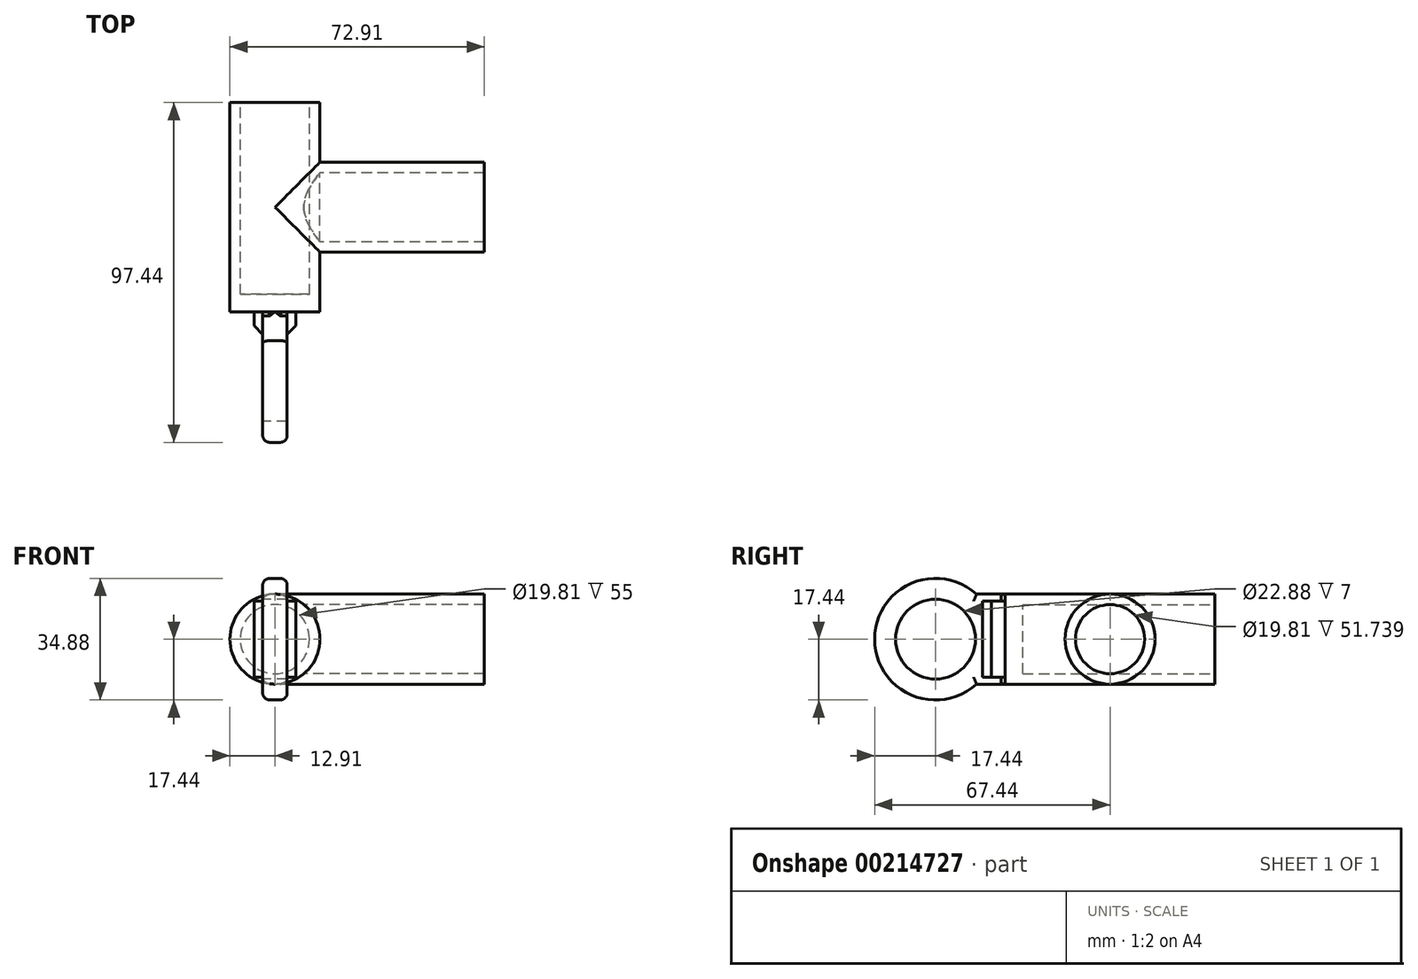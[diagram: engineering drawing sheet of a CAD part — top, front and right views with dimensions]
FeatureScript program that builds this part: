
annotation { "Feature Type Name" : "Feature", "Feature Type Description" : "" }
export const myFeature = defineFeature(function(context is Context, id is Id, definition is map)
    precondition{}
    {
        {
            assignVariable(context, id + "F0", {"name" : "ZZW", "anyValue" : 7});
        }
        {
            var Q0;
            Q0=qCreatedBy(makeId("Front.planeOp"),FACE);
            var sketch = newSketch(context, id + "F1", { "sketchPlane" : qUnion([Q0])});
            skCircle(sketch, "E0", {"center": v(0, 0) * mm, "radius": 9.9 * mm});
            skCircle(sketch, "E1", {"center": v(0, 0) * mm, "radius": 12.9 * mm});
            skSolve(sketch);
        }
        {
            var Q0;
            Q0=qSketchRegion(id+"F1",true);
            extrude(context, id + "F2", {"entities" : qUnion([Q0]), "depth" : 55 * mm});
        }
        {
            var Q0;
            Q0=makeQuery(id+"F2.opExtrude","CAP_FACE",FACE,{"disambiguationData":[OSD([sQuery(id+"F1.wireOp",EDGE,"E0"),sQuery(id+"F1.wireOp",EDGE,"E1")])],"isStart":false});
            var sketch = newSketch(context, id + "F3", { "sketchPlane" : qUnion([Q0])});
            skCircle(sketch, "E2", {"center": v(0, 0) * mm, "radius": 12.9 * mm});
            skSolve(sketch);
        }
        {
            var Q0;
            Q0=qSketchRegion(id+"F3",true);
            extrude(context, id + "F4", {"entities" : qUnion([Q0]), "operationType" : NewBodyOperationType.ADD, "depth" : 5 * mm});
        }
        {
            var Q0;
            Q0=qCreatedBy(makeId("Right.planeOp"),FACE);
            var sketch = newSketch(context, id + "F5", { "sketchPlane" : qUnion([Q0])});
            skLineSegment(sketch, "E3", {"start": v(0, 0) * mm, "end": v(0, -12.9) * mm, "construction": true});
            skLineSegment(sketch, "E4", {"start": v(0, -12.9) * mm, "end": v(-60, -12.9) * mm, "construction": true});
            skLineSegment(sketch, "E5", {"start": v(-60, 0) * mm, "end": v(-60, 12.9) * mm, "construction": true});
            skLineSegment(sketch, "E6", {"start": v(-60, -12.9) * mm, "end": v(-80, -12.9) * mm});
            skLineSegment(sketch, "E7", {"start": v(-80, -12.9) * mm, "end": v(-80, 12.9) * mm});
            skLineSegment(sketch, "E8", {"start": v(-80, 12.9) * mm, "end": v(-60, 12.9) * mm});
            skLineSegment(sketch, "E9", {"start": v(-60, -12.9) * mm, "end": v(-60, 12.9) * mm});
            skCircle(sketch, "E10", {"center": v(-80, 0) * mm, "radius": 11.44 * mm});
            skCircle(sketch, "E11", {"center": v(-80, 0) * mm, "radius": 17.44 * mm});
            skSolve(sketch);
        }
        {
            var Q0;
            {var subQ1=sQuery(id+"F5.wireOp",EDGE,"E7");var subQ5=sQuery(id+"F5.wireOp",EDGE,"E6");var subQ6=makeQuery(id+"F5.imprint","INTERSECT",VERTEX,{"derivedFrom":[subQ5,subQ1]});Q0=makeQuery(id+"F5.imprint","IMPRINT",FACE,{"disambiguationData":[TD([[makeQuery(id+"F5.imprint","IMPRINT",EDGE,{"disambiguationData":[TD([[subQ6,1.0]])],"derivedFrom":subQ5}),1.0]])]});}
            var Q1;
            {var subQ0=sQuery(id+"F5.wireOp",EDGE,"E9");Q1=makeQuery(id+"F5.imprint","IMPRINT",FACE,{"disambiguationData":[TD([[makeQuery(id+"F5.imprint","IMPRINT",EDGE,{"derivedFrom":subQ0}),1.0]])]});}
            var Q2;
            {var subQ1=sQuery(id+"F5.wireOp",EDGE,"E7");var subQ5=sQuery(id+"F5.wireOp",EDGE,"E6");var subQ6=makeQuery(id+"F5.imprint","INTERSECT",VERTEX,{"derivedFrom":[subQ5,subQ1]});Q2=makeQuery(id+"F5.imprint","IMPRINT",FACE,{"disambiguationData":[TD([[makeQuery(id+"F5.imprint","IMPRINT",EDGE,{"disambiguationData":[TD([[subQ6,1.0]])],"derivedFrom":subQ5}),-1.0]])]});}
            extrude(context, id + "F6", {"entities" : qUnion([Q0, Q1, Q2]), "operationType" : NewBodyOperationType.ADD, "depth" : (getVariable(context, 'ZZW') / 2) * mm, "hasSecondDirection" : true, "secondDirectionOppositeDirection" : true, "secondDirectionDepth" : (getVariable(context, 'ZZW') / 2) * mm});
        }
        {
            var Q0;
            {var subQ0=sQuery(id+"F5.wireOp",EDGE,"E9");var subQ1=sQuery(id+"F5.wireOp",EDGE,"E6");Q0=makeQuery(id+"F6.boolean.opBoolean","SPLIT",EDGE,{"disambiguationData":[TD([makeQuery(id+"F6.opExtrude","CAP_FACE",FACE,{"disambiguationData":[OSD([subQ1,sQuery(id+"F5.wireOp",EDGE,"E8"),subQ0,sQuery(id+"F5.wireOp",EDGE,"E10"),sQuery(id+"F5.wireOp",EDGE,"E11")])],"isStart":true})])],"derivedFrom":makeQuery(id+"F6.opExtrude","SWEPT_EDGE",EDGE,{"disambiguationData":[OSD([subQ1,subQ0])]})});}
            var Q1;
            {var subQ0=sQuery(id+"F5.wireOp",EDGE,"E6");var subQ1=sQuery(id+"F5.wireOp",EDGE,"E9");Q1=makeQuery(id+"F6.boolean.opBoolean","SPLIT",EDGE,{"disambiguationData":[TD([makeQuery(id+"F6.opExtrude","CAP_FACE",FACE,{"disambiguationData":[OSD([subQ0,sQuery(id+"F5.wireOp",EDGE,"E8"),subQ1,sQuery(id+"F5.wireOp",EDGE,"E10"),sQuery(id+"F5.wireOp",EDGE,"E11")])],"isStart":false})])],"derivedFrom":makeQuery(id+"F6.opExtrude","SWEPT_EDGE",EDGE,{"disambiguationData":[OSD([subQ0,subQ1])]})});}
            fillet(context, id + "F7", {"entities" : qUnion([Q0, Q1]), "radius" : 5 * mm, "tangentPropagation" : true, "allowEdgeOverflow" : false});
        }
        {
            var Q0;
            {var subQ0=sQuery(id+"F5.wireOp",EDGE,"E9");var subQ1=sQuery(id+"F5.wireOp",EDGE,"E8");Q0=makeQuery(id+"F6.boolean.opBoolean","SPLIT",EDGE,{"disambiguationData":[TD([makeQuery(id+"F6.opExtrude","CAP_FACE",FACE,{"disambiguationData":[OSD([sQuery(id+"F5.wireOp",EDGE,"E6"),subQ1,subQ0,sQuery(id+"F5.wireOp",EDGE,"E10"),sQuery(id+"F5.wireOp",EDGE,"E11")])],"isStart":true})])],"derivedFrom":makeQuery(id+"F6.opExtrude","SWEPT_EDGE",EDGE,{"disambiguationData":[OSD([subQ1,subQ0])]})});}
            var Q1;
            {var subQ0=sQuery(id+"F5.wireOp",EDGE,"E9");var subQ1=sQuery(id+"F5.wireOp",EDGE,"E8");Q1=makeQuery(id+"F6.boolean.opBoolean","SPLIT",EDGE,{"disambiguationData":[TD([makeQuery(id+"F6.opExtrude","CAP_FACE",FACE,{"disambiguationData":[OSD([sQuery(id+"F5.wireOp",EDGE,"E6"),subQ1,subQ0,sQuery(id+"F5.wireOp",EDGE,"E10"),sQuery(id+"F5.wireOp",EDGE,"E11")])],"isStart":false})])],"derivedFrom":makeQuery(id+"F6.opExtrude","SWEPT_EDGE",EDGE,{"disambiguationData":[OSD([subQ1,subQ0])]})});}
            fillet(context, id + "F8", {"entities" : qUnion([Q0, Q1]), "radius" : 5 * mm, "tangentPropagation" : true, "allowEdgeOverflow" : false});
        }
        {
            var Q0;
            Q0=makeQuery(id+"F6.opExtrude","CAP_EDGE",EDGE,{"disambiguationData":[OSD([sQuery(id+"F5.wireOp",EDGE,"E11")])],"isStart":true});
            fillet(context, id + "F9", {"entities" : qUnion([Q0]), "radius" : 2 * mm, "tangentPropagation" : true, "allowEdgeOverflow" : false});
        }
        {
            var Q0;
            Q0=makeQuery(id+"F6.opExtrude","CAP_EDGE",EDGE,{"disambiguationData":[OSD([sQuery(id+"F5.wireOp",EDGE,"E11")])],"isStart":false});
            fillet(context, id + "F10", {"entities" : qUnion([Q0]), "radius" : 2 * mm, "tangentPropagation" : true, "allowEdgeOverflow" : false});
        }
        {
            var Q0;
            Q0=makeQuery(id+"F6.opExtrude","CAP_EDGE",EDGE,{"disambiguationData":[OSD([sQuery(id+"F5.wireOp",EDGE,"E6")])],"isStart":false});
            fillet(context, id + "F11", {"entities" : qUnion([Q0]), "radius" : 2 * mm, "tangentPropagation" : true, "allowEdgeOverflow" : false});
        }
        {
            var Q0;
            Q0=makeQuery(id+"F6.opExtrude","CAP_EDGE",EDGE,{"disambiguationData":[OSD([sQuery(id+"F5.wireOp",EDGE,"E6")])],"isStart":true});
            fillet(context, id + "F12", {"entities" : qUnion([Q0]), "radius" : 2 * mm, "tangentPropagation" : true, "allowEdgeOverflow" : false});
        }
        {
            var Q0;
            Q0=makeQuery(id+"F6.opExtrude","CAP_EDGE",EDGE,{"disambiguationData":[OSD([sQuery(id+"F5.wireOp",EDGE,"E8")])],"isStart":true});
            fillet(context, id + "F13", {"entities" : qUnion([Q0]), "radius" : 2 * mm, "tangentPropagation" : true, "allowEdgeOverflow" : false});
        }
        {
            var Q0;
            Q0=makeQuery(id+"F6.opExtrude","CAP_EDGE",EDGE,{"disambiguationData":[OSD([sQuery(id+"F5.wireOp",EDGE,"E8")])],"isStart":false});
            fillet(context, id + "F14", {"entities" : qUnion([Q0]), "radius" : 2 * mm, "tangentPropagation" : true, "allowEdgeOverflow" : false});
        }
        {
            var Q0;
            Q0=qCreatedBy(makeId("Right.planeOp"),FACE);
            var sketch = newSketch(context, id + "F15", { "sketchPlane" : qUnion([Q0])});
            skLineSegment(sketch, "E12", {"start": v(0, 0) * mm, "end": v(-60, 0) * mm, "construction": true});
            skLineSegment(sketch, "E13", {"start": v(-60, 0) * mm, "end": v(-67, 0) * mm, "construction": true});
            skLineSegment(sketch, "E14", {"start": v(-67, 0) * mm, "end": v(-67, 10.9) * mm});
            skLineSegment(sketch, "E15", {"start": v(-67, 0) * mm, "end": v(-67, -10.9) * mm});
            skLineSegment(sketch, "E16", {"start": v(-67, -10.9) * mm, "end": v(-60, -10.9) * mm});
            skLineSegment(sketch, "E17", {"start": v(-60, -10.9) * mm, "end": v(-60, 10.9) * mm});
            skLineSegment(sketch, "E18", {"start": v(-60, 10.9) * mm, "end": v(-67, 10.9) * mm});
            skSolve(sketch);
        }
        {
            var Q0;
            Q0=qSketchRegion(id+"F15",true);
            extrude(context, id + "F16", {"entities" : qUnion([Q0]), "operationType" : NewBodyOperationType.ADD, "depth" : 6 * mm, "hasSecondDirection" : true, "secondDirectionOppositeDirection" : true, "secondDirectionDepth" : 6 * mm});
        }
        {
            var Q0;
            Q0=makeQuery(id+"F16.opExtrude","CAP_EDGE",EDGE,{"disambiguationData":[OSD([sQuery(id+"F15.wireOp",EDGE,"E14"),sQuery(id+"F15.wireOp",EDGE,"E15")])],"isStart":false});
            var Q1;
            Q1=makeQuery(id+"F16.opExtrude","CAP_EDGE",EDGE,{"disambiguationData":[OSD([sQuery(id+"F15.wireOp",EDGE,"E14"),sQuery(id+"F15.wireOp",EDGE,"E15")])],"isStart":true});
            chamfer(context, id + "F17", {"entities" : qUnion([Q0, Q1]), "width" : 3 * mm, "tangentPropagation" : true});
        }
        {
            var Q0;
            Q0=qCreatedBy(makeId("Right.planeOp"),FACE);
            var sketch = newSketch(context, id + "F18", { "sketchPlane" : qUnion([Q0])});
            skCircle(sketch, "E19", {"center": v(-30, 0) * mm, "radius": 9.9 * mm});
            skCircle(sketch, "E20", {"center": v(-30, 0) * mm, "radius": 12.9 * mm});
            skSolve(sketch);
        }
        {
            var Q0;
            Q0=qSketchRegion(id+"F18",true);
            extrude(context, id + "F19", {"entities" : qUnion([Q0]), "operationType" : NewBodyOperationType.ADD, "depth" : 60 * mm});
        }
        {
            var Q0;
            Q0=makeQuery(id+"F4.opExtrude","CAP_FACE",FACE,{"disambiguationData":[OSD([sQuery(id+"F3.wireOp",EDGE,"E2")])],"isStart":true});
            var sketch = newSketch(context, id + "F20", { "sketchPlane" : qUnion([Q0])});
            skCircle(sketch, "E21", {"center": v(0, 0) * mm, "radius": 9.9 * mm});
            skSolve(sketch);
        }
        {
            var Q0;
            Q0=qSketchRegion(id+"F20",true);
            extrude(context, id + "F21", {"entities" : qUnion([Q0]), "operationType" : NewBodyOperationType.REMOVE, "depth" : 60 * mm});
        }
    });
